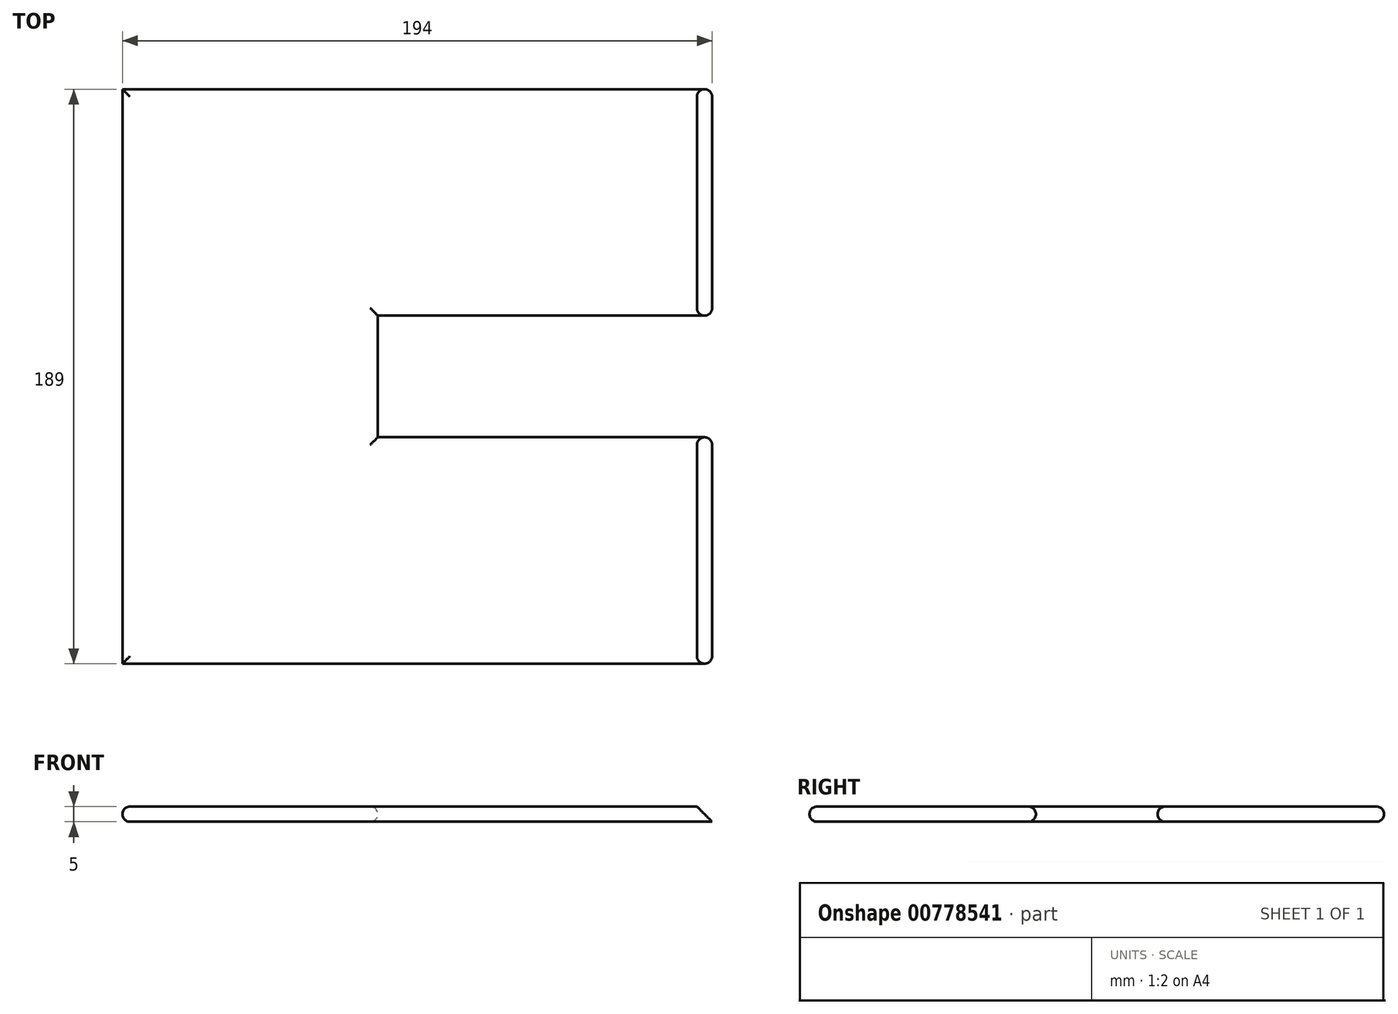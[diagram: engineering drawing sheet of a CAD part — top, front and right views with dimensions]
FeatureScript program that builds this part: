
annotation { "Feature Type Name" : "Feature", "Feature Type Description" : "" }
export const myFeature = defineFeature(function(context is Context, id is Id, definition is map)
    precondition{}
    {
        {
            var Q0;
            Q0=qCreatedBy(makeId("Top.planeOp"),FACE);
            var sketch = newSketch(context, id + "F0", { "sketchPlane" : qUnion([Q0])});
            skLineSegment(sketch, "E0.bottom", {"start": v(97, -94.5) * mm, "end": v(-97, -94.5) * mm});
            skLineSegment(sketch, "E0.top", {"start": v(97, 94.5) * mm, "end": v(-97, 94.5) * mm});
            skLineSegment(sketch, "E0.left", {"start": v(97, -94.5) * mm, "end": v(97, 94.5) * mm});
            skLineSegment(sketch, "E0.right", {"start": v(-97, -94.5) * mm, "end": v(-97, 94.5) * mm});
            skPoint(sketch, "E0.middle", {"position": v(0, 0) * mm});
            skLineSegment(sketch, "E1.bottom", {"start": v(207, -20) * mm, "end": v(-13, -20) * mm});
            skLineSegment(sketch, "E1.top", {"start": v(207, 20) * mm, "end": v(-13, 20) * mm});
            skLineSegment(sketch, "E1.left", {"start": v(207, -20) * mm, "end": v(207, 20) * mm});
            skLineSegment(sketch, "E1.right", {"start": v(-13, -20) * mm, "end": v(-13, 20) * mm});
            skPoint(sketch, "E1.middle", {"position": v(97, 0) * mm});
            skSolve(sketch);
        }
        {
            var Q0;
            {var subQ4=sQuery(id+"F0.wireOp",EDGE,"E0.bottom");Q0=makeQuery(id+"F0.imprint","IMPRINT",FACE,{"disambiguationData":[TD([[makeQuery(id+"F0.imprint","IMPRINT",EDGE,{"derivedFrom":subQ4}),-1.0]])]});}
            extrude(context, id + "F1", {"entities" : qUnion([Q0]), "depth" : 5 * mm, "offsetDistance" : 25 * mm});
        }
        {
            var Q0;
            {var subQ0=sQuery(id+"F0.wireOp",EDGE,"E0.left");Q0=makeQuery(id+"F1.opExtrude","CAP_EDGE",EDGE,{"disambiguationData":[OSD([subQ0]),TDD([makeQuery(id+"F0.imprint","IMPRINT",EDGE,{"disambiguationData":[TD([[makeQuery(id+"F0.imprint","INTERSECT",VERTEX,{"derivedFrom":[sQuery(id+"F0.wireOp",EDGE,"E0.bottom"),subQ0]}),-1.0]])],"derivedFrom":subQ0})])],"isStart":false});}
            var Q1;
            {var subQ0=sQuery(id+"F0.wireOp",EDGE,"E0.left");Q1=makeQuery(id+"F1.opExtrude","CAP_EDGE",EDGE,{"disambiguationData":[OSD([subQ0]),TDD([makeQuery(id+"F0.imprint","IMPRINT",EDGE,{"disambiguationData":[TD([[makeQuery(id+"F0.imprint","INTERSECT",VERTEX,{"derivedFrom":[sQuery(id+"F0.wireOp",EDGE,"E0.top"),subQ0]}),1.0]])],"derivedFrom":subQ0})])],"isStart":false});}
            chamfer(context, id + "F2", {"entities" : qUnion([Q0, Q1]), "width" : 5 * mm, "tangentPropagation" : true});
        }
        {
            var Q0;
            Q0=makeQuery(id+"F1.opExtrude","CAP_EDGE",EDGE,{"disambiguationData":[OSD([sQuery(id+"F0.wireOp",EDGE,"E1.right")])],"isStart":false});
            var Q1;
            Q1=makeQuery(id+"F1.opExtrude","CAP_EDGE",EDGE,{"disambiguationData":[OSD([sQuery(id+"F0.wireOp",EDGE,"E1.top")])],"isStart":false});
            var Q2;
            Q2=makeQuery(id+"F1.opExtrude","CAP_EDGE",EDGE,{"disambiguationData":[OSD([sQuery(id+"F0.wireOp",EDGE,"E1.bottom")])],"isStart":false});
            var Q3;
            Q3=makeQuery(id+"F1.opExtrude","CAP_EDGE",EDGE,{"disambiguationData":[OSD([sQuery(id+"F0.wireOp",EDGE,"E1.bottom")])],"isStart":true});
            var Q4;
            Q4=makeQuery(id+"F1.opExtrude","CAP_EDGE",EDGE,{"disambiguationData":[OSD([sQuery(id+"F0.wireOp",EDGE,"E1.right")])],"isStart":true});
            var Q5;
            Q5=makeQuery(id+"F1.opExtrude","CAP_EDGE",EDGE,{"disambiguationData":[OSD([sQuery(id+"F0.wireOp",EDGE,"E1.top")])],"isStart":true});
            var Q6;
            Q6=makeQuery(id+"F1.opExtrude","CAP_EDGE",EDGE,{"disambiguationData":[OSD([sQuery(id+"F0.wireOp",EDGE,"E0.bottom")])],"isStart":true});
            var Q7;
            Q7=makeQuery(id+"F1.opExtrude","CAP_EDGE",EDGE,{"disambiguationData":[OSD([sQuery(id+"F0.wireOp",EDGE,"E0.right")])],"isStart":true});
            var Q8;
            Q8=makeQuery(id+"F1.opExtrude","CAP_EDGE",EDGE,{"disambiguationData":[OSD([sQuery(id+"F0.wireOp",EDGE,"E0.top")])],"isStart":true});
            var Q9;
            Q9=makeQuery(id+"F1.opExtrude","CAP_EDGE",EDGE,{"disambiguationData":[OSD([sQuery(id+"F0.wireOp",EDGE,"E0.right")])],"isStart":false});
            var Q10;
            Q10=makeQuery(id+"F1.opExtrude","CAP_EDGE",EDGE,{"disambiguationData":[OSD([sQuery(id+"F0.wireOp",EDGE,"E0.top")])],"isStart":false});
            var Q11;
            Q11=makeQuery(id+"F1.opExtrude","CAP_EDGE",EDGE,{"disambiguationData":[OSD([sQuery(id+"F0.wireOp",EDGE,"E0.bottom")])],"isStart":false});
            fillet(context, id + "F3", {"entities" : qUnion([Q0, Q1, Q2, Q3, Q4, Q5, Q6, Q7, Q8, Q9, Q10, Q11]), "radius" : 2.5 * mm, "tangentPropagation" : true, "allowEdgeOverflow" : false});
        }
    });
